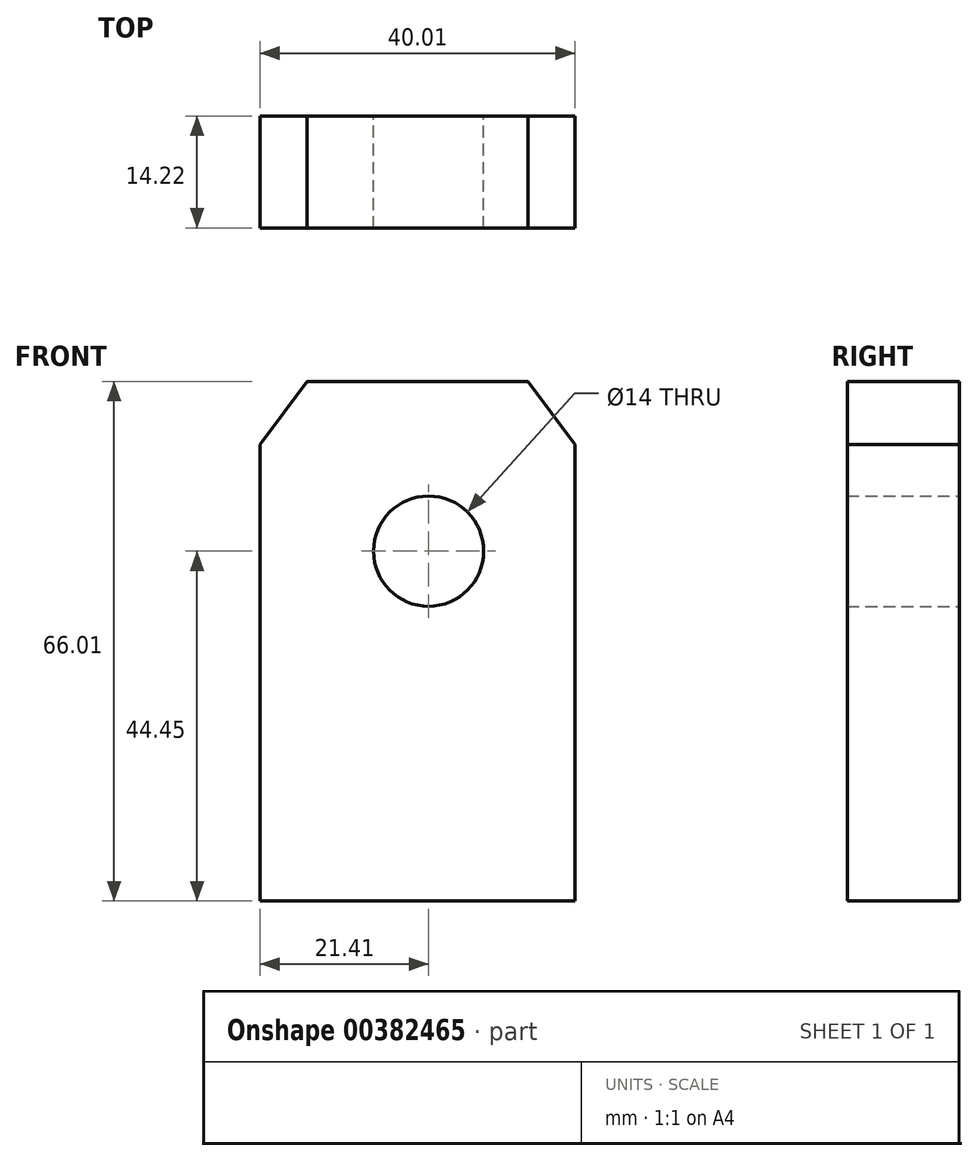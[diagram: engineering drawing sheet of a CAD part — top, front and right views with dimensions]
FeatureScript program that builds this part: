
annotation { "Feature Type Name" : "Feature", "Feature Type Description" : "" }
export const myFeature = defineFeature(function(context is Context, id is Id, definition is map)
    precondition{}
    {
        {
            var Q0;
            Q0=qCreatedBy(makeId("Front.planeOp"),FACE);
            var sketch = newSketch(context, id + "F0", { "sketchPlane" : qUnion([Q0])});
            skLineSegment(sketch, "E0", {"start": v(-21.4, 0) * mm, "end": v(18.6, 0) * mm});
            skLineSegment(sketch, "E1", {"start": v(-21.4, 0) * mm, "end": v(-21.4, 57.99) * mm});
            skLineSegment(sketch, "E2", {"start": v(18.6, 57.99) * mm, "end": v(18.6, 0) * mm});
            skLineSegment(sketch, "E3", {"start": v(-21.4, 57.99) * mm, "end": v(-15.43, 66.01) * mm});
            skLineSegment(sketch, "E4", {"start": v(-15.43, 66.01) * mm, "end": v(12.62, 66.01) * mm});
            skLineSegment(sketch, "E5", {"start": v(12.62, 66.01) * mm, "end": v(18.6, 57.99) * mm});
            skCircle(sketch, "E6", {"center": v(0, 44.45) * mm, "radius": 7 * mm});
            skSolve(sketch);
        }
        {
            var Q0;
            Q0=makeQuery(id+"F0.imprint","IMPRINT",FACE,{"disambiguationData":[TD([[makeQuery(id+"F0.imprint","IMPRINT",EDGE,{"derivedFrom":sQuery(id+"F0.wireOp",EDGE,"E0")}),1.0]])]});
            extrude(context, id + "F1", {"entities" : qUnion([Q0]), "depth" : 14.22 * mm});
        }
    });
